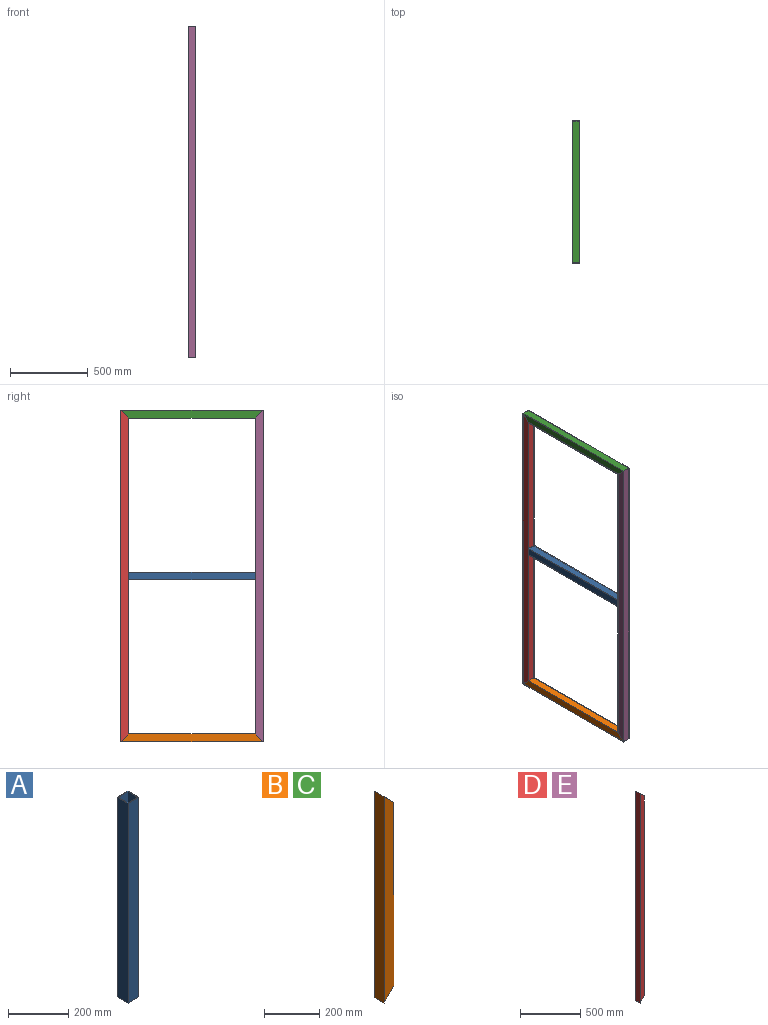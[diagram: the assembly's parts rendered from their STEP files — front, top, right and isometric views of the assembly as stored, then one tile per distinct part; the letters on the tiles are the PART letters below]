
ASSEMBLY  parts=5 mates=4
PART A: 10 faces, bbox 50.8x50.8x812.8 mm
  f0: plane 812.8x50.8mm, normal (0,-1,0), area 41290.2mm2, adj f1,f7,f8,f9
  f1: plane 812.8x50.8mm, normal (1,0,0), area 41290.2mm2, adj f0,f2,f8,f9
  f2: plane 812.8x50.8mm, normal (0,1,0), area 41290.2mm2, adj f1,f7,f8,f9
  f3: plane 812.8x44.6mm, normal (0,1,0), area 36252.8mm2, adj f4,f6,f8,f9
  f4: plane 812.8x44.6mm, normal (1,0,0), area 36252.8mm2, adj f3,f5,f8,f9
  f5: plane 812.8x44.6mm, normal (0,-1,0), area 36252.8mm2, adj f4,f6,f8,f9
  f6: plane 812.8x44.6mm, normal (-1,0,0), area 36252.8mm2, adj f3,f5,f8,f9
  f7: plane 812.8x50.8mm, normal (-1,0,0), area 41290.2mm2, adj f0,f2,f8,f9
  f8: plane 50.8x50.8mm, normal (0,0,1), area 591.3mm2, adj f0,f1,f2,f3,f4,f5,f6,f7
  f9: plane 50.8x50.8mm, normal (0,0,-1), area 591.3mm2, adj f0,f1,f2,f3,f4,f5,f6,f7
PART B: 10 faces, bbox 50.8x50.8x914.4 mm
  f0: plane 914.4x50.8mm, normal (0,-1,0), area 43870.9mm2, adj f1,f7,f8,f9
  f1: plane 812.8x50.8mm, normal (1,0,0), area 41290.2mm2, adj f0,f2,f8,f9
  f2: plane 914.4x50.8mm, normal (0,1,0), area 43870.9mm2, adj f1,f7,f8,f9
  f3: plane 908.2x44.6mm, normal (0,1,0), area 38518.6mm2, adj f4,f6,f8,f9
  f4: plane 908.2x44.6mm, normal (1,0,0), area 40508mm2, adj f3,f5,f8,f9
  f5: plane 908.2x44.6mm, normal (0,-1,0), area 38518.6mm2, adj f4,f6,f8,f9
  f6: plane 819x44.6mm, normal (-1,0,0), area 36529.3mm2, adj f3,f5,f8,f9
  f7: plane 914.4x50.8mm, normal (-1,0,0), area 46451.5mm2, adj f0,f2,f8,f9
  f8: plane 50.8x50.8mm, normal (0.71,0,-0.71), area 836.2mm2, adj f0,f1,f2,f3,f4,f5,f6,f7
  f9: plane 50.8x50.8mm, normal (0.71,0,0.71), area 836.2mm2, adj f0,f1,f2,f3,f4,f5,f6,f7
PART C: same geometry as B
PART D: 10 faces, bbox 50.8x50.8x2133.6 mm
  f0: plane 2133.6x50.8mm, normal (0,-1,0), area 105806.2mm2, adj f1,f7,f8,f9
  f1: plane 2032x50.8mm, normal (1,0,0), area 103225.6mm2, adj f0,f2,f8,f9
  f2: plane 2133.6x50.8mm, normal (0,1,0), area 105806.2mm2, adj f1,f7,f8,f9
  f3: plane 2127.4x44.6mm, normal (0,1,0), area 92897.9mm2, adj f4,f6,f8,f9
  f4: plane 2127.4x44.6mm, normal (1,0,0), area 94887.3mm2, adj f3,f5,f8,f9
  f5: plane 2127.4x44.6mm, normal (0,-1,0), area 92897.9mm2, adj f4,f6,f8,f9
  f6: plane 2038.2x44.6mm, normal (-1,0,0), area 90908.5mm2, adj f3,f5,f8,f9
  f7: plane 2133.6x50.8mm, normal (-1,0,0), area 108386.9mm2, adj f0,f2,f8,f9
  f8: plane 50.8x50.8mm, normal (0.71,0,-0.71), area 836.2mm2, adj f0,f1,f2,f3,f4,f5,f6,f7
  f9: plane 50.8x50.8mm, normal (0.71,0,0.71), area 836.2mm2, adj f0,f1,f2,f3,f4,f5,f6,f7
PART E: same geometry as D
PLACE A rot(axis=(1,0,0),90deg) t=(0,812.8,1016)mm
PLACE B rot(axis=(0.58,-0.58,0.58),120deg) t=(0,863.6,-25.4)mm
PLACE C rot(axis=(0.58,0.58,-0.58),120deg) t=(0,863.6,2057.4)mm
PLACE D rot(axis=(0,0,-1),90deg) t=(0,838.2,-50.8)mm
PLACE E rot(axis=(0,0,1),90deg) t=(0,-25.4,-50.8)mm
MATE fastened C.f8 <-> D.f9  axis (0,0.71,-0.71) through (0,863.6,2082.8)mm
MATE fastened E.f8 <-> B.f9  axis (0,0.71,-0.71) through (0,-50.8,-50.8)mm
MATE fastened C.f9 <-> E.f9  axis (0,-0.71,-0.71) through (0,-50.8,2082.8)mm
MATE fastened A.f8 <-> E.f1  axis (0,-1,0) through (0,0,1016)mm
